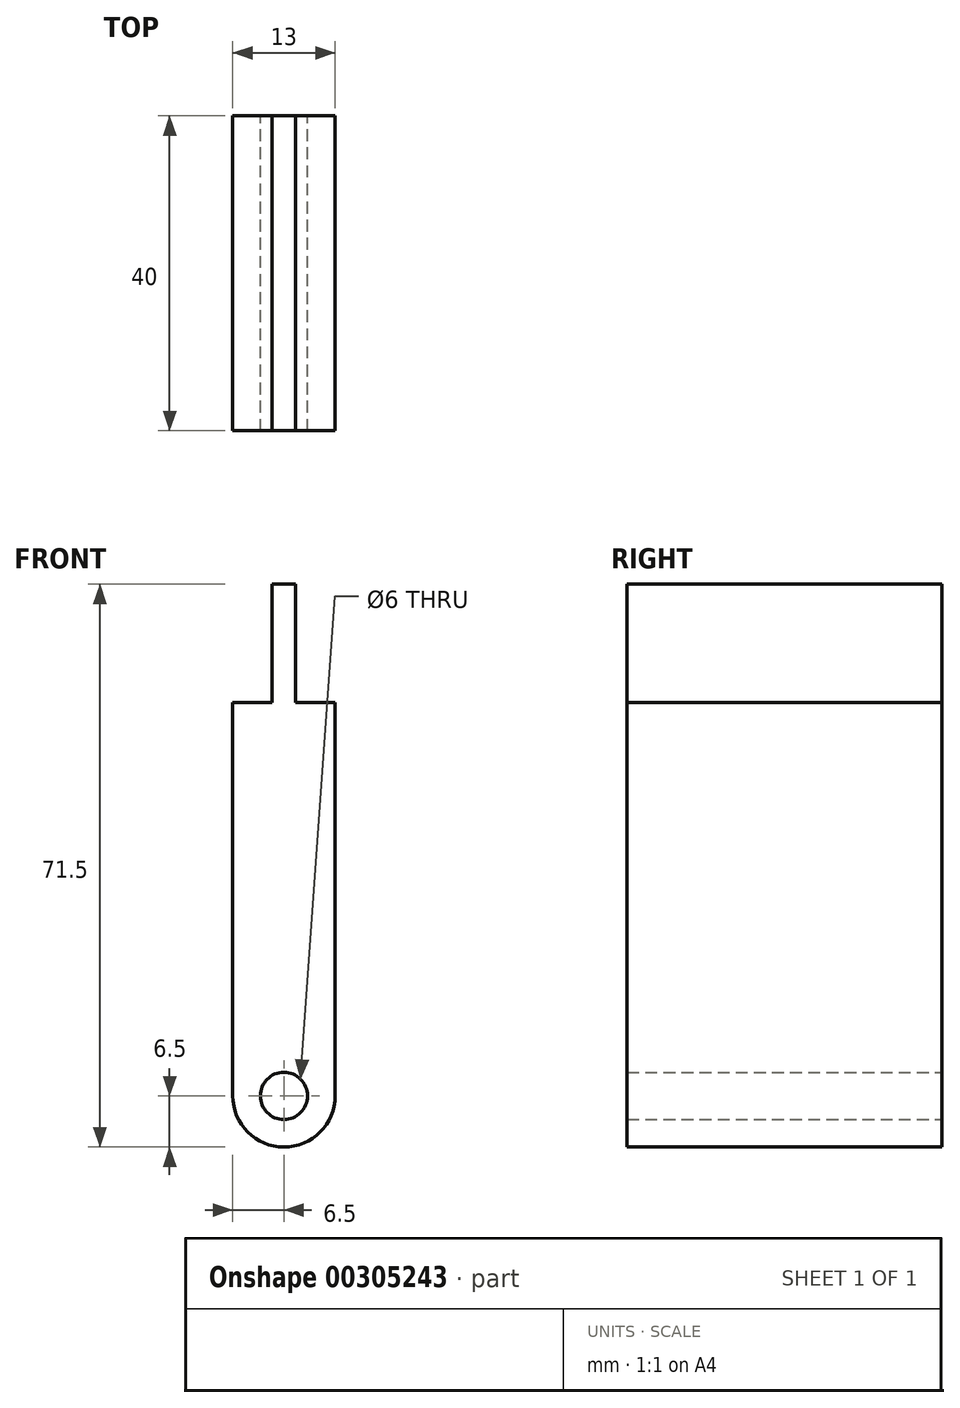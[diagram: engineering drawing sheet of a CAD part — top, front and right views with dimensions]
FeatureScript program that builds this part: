
annotation { "Feature Type Name" : "Feature", "Feature Type Description" : "" }
export const myFeature = defineFeature(function(context is Context, id is Id, definition is map)
    precondition{}
    {
        {
            var Q0;
            Q0=qCreatedBy(makeId("Front.planeOp"),FACE);
            var sketch = newSketch(context, id + "F0", { "sketchPlane" : qUnion([Q0])});
            skArc(sketch, "E0", {"start": v(-6.5, 0) * mm, "mid": v(0, -6.5) * mm, "end": v(6.5, 0) * mm});
            skLineSegment(sketch, "E1", {"start": v(-6.5, 0) * mm, "end": v(-6.5, 50) * mm});
            skLineSegment(sketch, "E2", {"start": v(-6.5, 50) * mm, "end": v(-1.5, 50) * mm});
            skLineSegment(sketch, "E3", {"start": v(-1.5, 50) * mm, "end": v(-1.5, 65) * mm});
            skLineSegment(sketch, "E4", {"start": v(-1.5, 65) * mm, "end": v(1.5, 65) * mm});
            skLineSegment(sketch, "E5", {"start": v(1.5, 65) * mm, "end": v(1.5, 50) * mm});
            skLineSegment(sketch, "E6", {"start": v(1.5, 50) * mm, "end": v(6.5, 50) * mm});
            skLineSegment(sketch, "E7", {"start": v(6.5, 50) * mm, "end": v(6.5, 0) * mm});
            skCircle(sketch, "E8", {"center": v(0, 0) * mm, "radius": 3 * mm});
            skSolve(sketch);
        }
        {
            var Q0;
            Q0=makeQuery(id+"F0.imprint","IMPRINT",FACE,{"disambiguationData":[TD([[makeQuery(id+"F0.imprint","IMPRINT",EDGE,{"derivedFrom":sQuery(id+"F0.wireOp",EDGE,"E0")}),1.0]])]});
            extrude(context, id + "F1", {"entities" : qUnion([Q0]), "depth" : 40 * mm});
        }
    });
